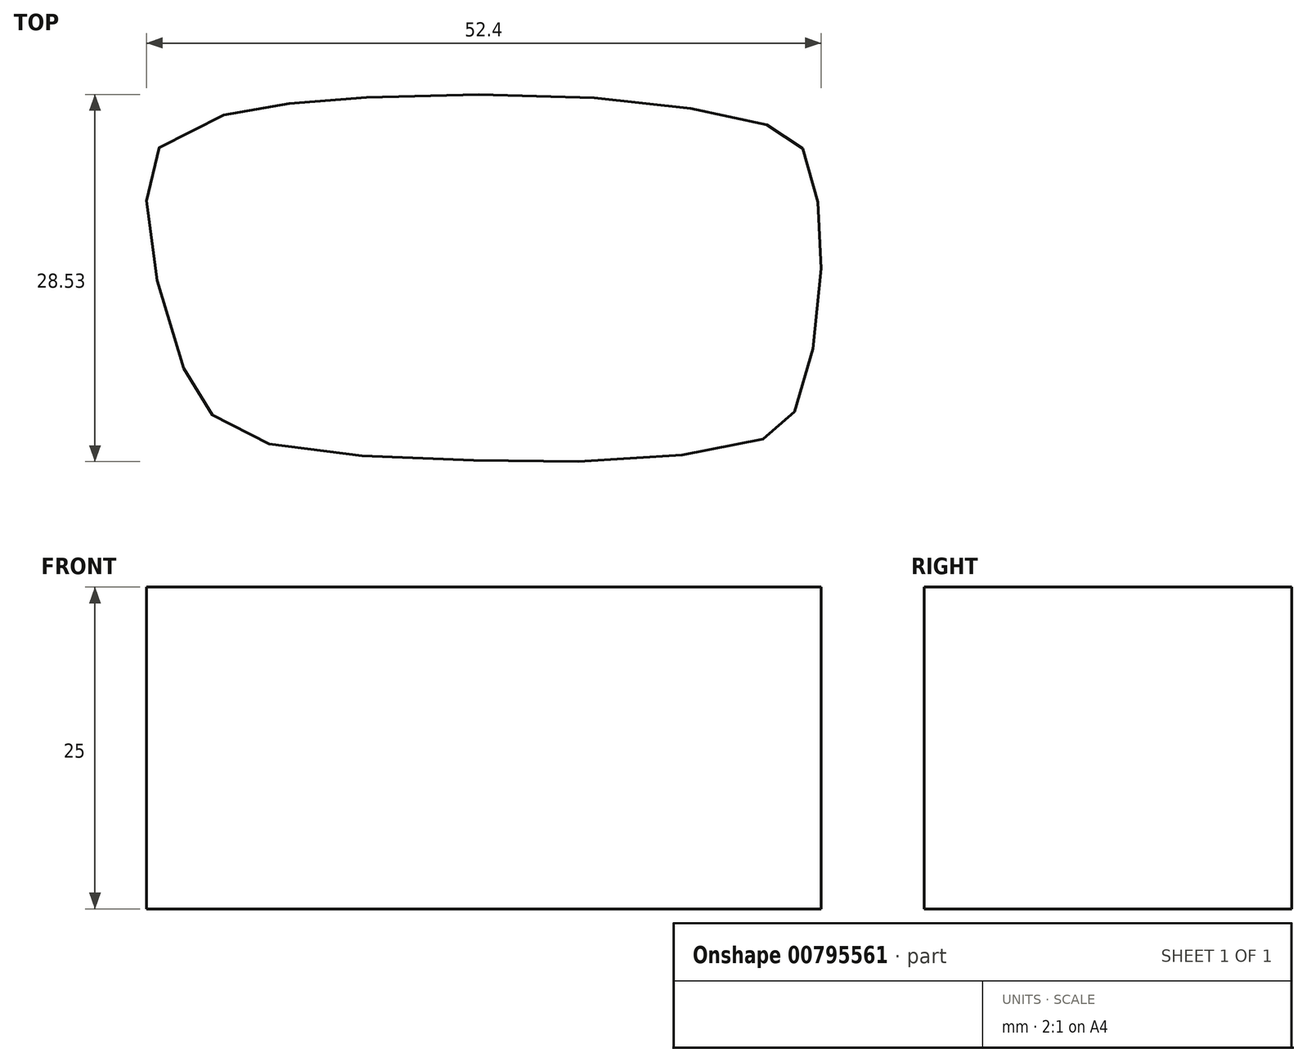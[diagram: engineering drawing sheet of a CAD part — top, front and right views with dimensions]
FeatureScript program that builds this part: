
annotation { "Feature Type Name" : "Feature", "Feature Type Description" : "" }
export const myFeature = defineFeature(function(context is Context, id is Id, definition is map)
    precondition{}
    {
        {
            var Q0;
            Q0=qCreatedBy(makeId("Top.planeOp"),FACE);
            var sketch = newSketch(context, id + "F0", { "sketchPlane" : qUnion([Q0])});
            skFitSpline(sketch, "E0", {"points": [v(17.22, 16.2) * mm, v(31.36, 16.37) * mm, v(42.18, 15.37) * mm, v(48.45, 14.03) * mm, v(50.34, 12.93) * mm, v(51.44, 11.67) * mm, v(52.26, 7.98) * mm, v(52.52, 3.27) * mm, v(51.84, -3.52) * mm, v(50.53, -8.03) * mm, v(49.43, -9.47) * mm, v(47.2, -10.6) * mm, v(37.87, -11.91) * mm, v(26.33, -12) * mm, v(13.67, -11.36) * mm, v(7.04, -9.78) * mm, v(4.51, -7.65) * mm, v(2.9, -4.54) * mm, v(0.45, 4.36) * mm, v(0.18, 9.56) * mm, v(1.19, 12.4) * mm, v(6.27, 14.88) * mm, v(10.91, 15.69) * mm, v(17.22, 16.2) * mm]});
            skLineSegment(sketch, "E1.0", {"start": v(-0.21, 6.26) * mm, "end": v(51.76, 7.98) * mm, "construction": true});
            skLineSegment(sketch, "E1.1", {"start": v(-0.21, 6.26) * mm, "end": v(-0.32, 9.56) * mm, "construction": true});
            skFitSpline(sketch, "E2.0", {"points": [v(14.97, 18.07) * mm, v(17.03, 18.2) * mm, v(19.98, 18.33) * mm, v(23.26, 18.42) * mm, v(26.7, 18.46) * mm, v(29.55, 18.43) * mm, v(31.75, 18.36) * mm, v(33.86, 18.26) * mm, v(36.36, 18.08) * mm, v(39.16, 17.8) * mm, v(41.37, 17.51) * mm, v(43.07, 17.27) * mm, v(44.32, 17.07) * mm, v(45.53, 16.85) * mm, v(46.68, 16.62) * mm, v(47.75, 16.35) * mm, v(48.75, 16.06) * mm, v(49.66, 15.7) * mm, v(50.31, 15.37) * mm, v(50.77, 15.09) * mm, v(51.08, 14.88) * mm, v(51.31, 14.7) * mm, v(51.49, 14.58) * mm, v(51.65, 14.45) * mm, v(51.87, 14.27) * mm, v(52.15, 14.02) * mm, v(52.45, 13.72) * mm, v(52.74, 13.37) * mm, v(52.97, 13.03) * mm, v(53.13, 12.74) * mm, v(53.29, 12.44) * mm, v(53.45, 12.05) * mm, v(53.61, 11.59) * mm, v(53.75, 11.12) * mm, v(53.9, 10.48) * mm, v(54.05, 9.67) * mm, v(54.19, 8.7) * mm, v(54.3, 7.77) * mm, v(54.4, 6.83) * mm, v(54.47, 5.88) * mm, v(54.51, 4.9) * mm, v(54.53, 3.89) * mm, v(54.51, 2.81) * mm, v(54.45, 1.3) * mm, v(54.29, -0.67) * mm, v(53.97, -3.06) * mm, v(53.53, -5.34) * mm, v(53.07, -7.05) * mm, v(52.64, -8.26) * mm, v(52.26, -9.1) * mm, v(51.88, -9.72) * mm, v(51.54, -10.17) * mm, v(51.27, -10.48) * mm, v(51.04, -10.72) * mm, v(50.84, -10.9) * mm, v(50.65, -11.06) * mm, v(50.4, -11.26) * mm, v(49.95, -11.58) * mm, v(49.32, -11.94) * mm, v(48.45, -12.3) * mm, v(47.45, -12.62) * mm, v(45.94, -12.99) * mm, v(43.76, -13.36) * mm, v(40.8, -13.7) * mm, v(37.75, -13.94) * mm, v(34.81, -14.06) * mm, v(31.92, -14.09) * mm, v(29, -14.06) * mm, v(26.03, -13.99) * mm, v(22.89, -13.91) * mm, v(19.7, -13.8) * mm, v(16.58, -13.64) * mm, v(13.62, -13.4) * mm, v(10.93, -13.04) * mm, v(8.91, -12.6) * mm, v(7.43, -12.14) * mm, v(6.56, -11.78) * mm, v(5.9, -11.44) * mm, v(5.28, -11.07) * mm, v(4.29, -10.37) * mm, v(3.38, -9.47) * mm, v(2.68, -8.55) * mm, v(2.2, -7.82) * mm, v(1.77, -7.02) * mm, v(1.38, -6.15) * mm, v(1, -5.18) * mm, v(0.6, -4.06) * mm, v(0.2, -2.82) * mm, v(-0.34, -1.05) * mm, v(-0.85, 0.82) * mm, v(-1.27, 2.66) * mm, v(-1.52, 4) * mm, v(-1.7, 5.24) * mm, v(-1.83, 6.4) * mm, v(-1.88, 7.47) * mm, v(-1.88, 8.47) * mm, v(-1.85, 9.16) * mm, v(-1.82, 9.6) * mm, v(-1.8, 9.9) * mm, v(-1.75, 10.42) * mm, v(-1.63, 11.23) * mm, v(-1.3, 12.3) * mm, v(-0.84, 13.1) * mm, v(-0.44, 13.59) * mm, v(-0.15, 13.9) * mm, v(0.24, 14.27) * mm, v(0.73, 14.64) * mm, v(1.42, 15.1) * mm, v(2.32, 15.58) * mm, v(3.46, 16.07) * mm, v(4.6, 16.48) * mm, v(5.73, 16.82) * mm, v(6.79, 17.08) * mm, v(7.8, 17.29) * mm, v(8.76, 17.44) * mm, v(9.69, 17.57) * mm, v(10.6, 17.67) * mm, v(11.52, 17.77) * mm, v(12.48, 17.86) * mm, v(13.5, 17.95) * mm, v(14.97, 18.07) * mm, v(17.03, 18.2) * mm, v(19.98, 18.33) * mm, v(14.97, 18.07) * mm]});
            skFitSpline(sketch, "E3.0", {"points": [v(14.76, 15.35) * mm, v(17.17, 15.5) * mm, v(20.08, 15.64) * mm, v(23.31, 15.72) * mm, v(26.7, 15.76) * mm, v(29.5, 15.73) * mm, v(31.64, 15.66) * mm, v(33.7, 15.56) * mm, v(36.13, 15.4) * mm, v(38.85, 15.12) * mm, v(41, 14.84) * mm, v(42.66, 14.6) * mm, v(44.28, 14.34) * mm, v(45.77, 14.06) * mm, v(47.06, 13.75) * mm, v(47.9, 13.5) * mm, v(48.56, 13.23) * mm, v(49.09, 12.96) * mm, v(49.46, 12.72) * mm, v(49.73, 12.52) * mm, v(49.94, 12.36) * mm, v(50.13, 12.2) * mm, v(50.35, 12) * mm, v(50.54, 11.8) * mm, v(50.7, 11.56) * mm, v(50.82, 11.35) * mm, v(50.93, 11.09) * mm, v(51.07, 10.68) * mm, v(51.23, 10.07) * mm, v(51.38, 9.24) * mm, v(51.51, 8.36) * mm, v(51.62, 7.47) * mm, v(51.7, 6.6) * mm, v(51.77, 5.72) * mm, v(51.81, 4.82) * mm, v(51.83, 3.89) * mm, v(51.81, 2.9) * mm, v(51.75, 1.48) * mm, v(51.6, -0.38) * mm, v(51.3, -2.64) * mm, v(50.9, -4.75) * mm, v(50.49, -6.27) * mm, v(50.13, -7.25) * mm, v(49.85, -7.85) * mm, v(49.58, -8.3) * mm, v(49.35, -8.59) * mm, v(49.14, -8.8) * mm, v(48.96, -8.95) * mm, v(48.78, -9.1) * mm, v(48.51, -9.29) * mm, v(48.13, -9.5) * mm, v(47.53, -9.77) * mm, v(46.75, -10.02) * mm, v(45.76, -10.25) * mm, v(44.61, -10.47) * mm, v(42.91, -10.74) * mm, v(40.55, -11.02) * mm, v(37.6, -11.25) * mm, v(34.75, -11.36) * mm, v(31.92, -11.39) * mm, v(29.06, -11.36) * mm, v(26.09, -11.3) * mm, v(22.96, -11.22) * mm, v(19.82, -11.1) * mm, v(16.76, -10.94) * mm, v(13.9, -10.7) * mm, v(11.37, -10.37) * mm, v(9.21, -9.9) * mm, v(7.77, -9.38) * mm, v(6.85, -8.88) * mm, v(6.25, -8.45) * mm, v(5.73, -8) * mm, v(5.28, -7.5) * mm, v(4.88, -6.98) * mm, v(4.53, -6.45) * mm, v(4.2, -5.84) * mm, v(3.88, -5.12) * mm, v(3.53, -4.24) * mm, v(3.16, -3.2) * mm, v(2.77, -2) * mm, v(2.26, -0.31) * mm, v(1.65, 1.94) * mm, v(1.2, 4.08) * mm, v(0.97, 5.58) * mm, v(0.87, 6.6) * mm, v(0.82, 7.54) * mm, v(0.82, 8.41) * mm, v(0.85, 9.22) * mm, v(0.91, 9.98) * mm, v(1.02, 10.65) * mm, v(1.2, 11.21) * mm, v(1.44, 11.63) * mm, v(1.71, 11.95) * mm, v(2.06, 12.27) * mm, v(2.63, 12.68) * mm, v(3.49, 13.14) * mm, v(4.44, 13.55) * mm, v(5.45, 13.91) * mm, v(6.45, 14.21) * mm, v(7.39, 14.45) * mm, v(8.28, 14.63) * mm, v(9.44, 14.82) * mm, v(10.59, 14.95) * mm, v(11.8, 15.08) * mm, v(13.05, 15.2) * mm, v(14.76, 15.35) * mm, v(17.17, 15.5) * mm, v(20.08, 15.64) * mm, v(14.76, 15.35) * mm]});
            skSolve(sketch);
        }
        {
            var Q0;
            Q0=makeQuery(id+"F0.imprint","IMPRINT",FACE,{"disambiguationData":[TD([[makeQuery(id+"F0.imprint","IMPRINT",EDGE,{"derivedFrom":sQuery(id+"F0.wireOp",EDGE,"E0")}),-1.0]])]});
            var Q1;
            Q1=makeQuery(id+"F0.imprint","IMPRINT",FACE,{"disambiguationData":[TD([[makeQuery(id+"F0.imprint","IMPRINT",EDGE,{"derivedFrom":sQuery(id+"F0.wireOp",EDGE,"E0")}),1.0]])]});
            extrude(context, id + "F1", {"entities" : qUnion([Q0, Q1]), "endBound" : BoundingType.SYMMETRIC, "depth" : 25 * mm, "offsetDistance" : 25 * mm});
        }
    });
